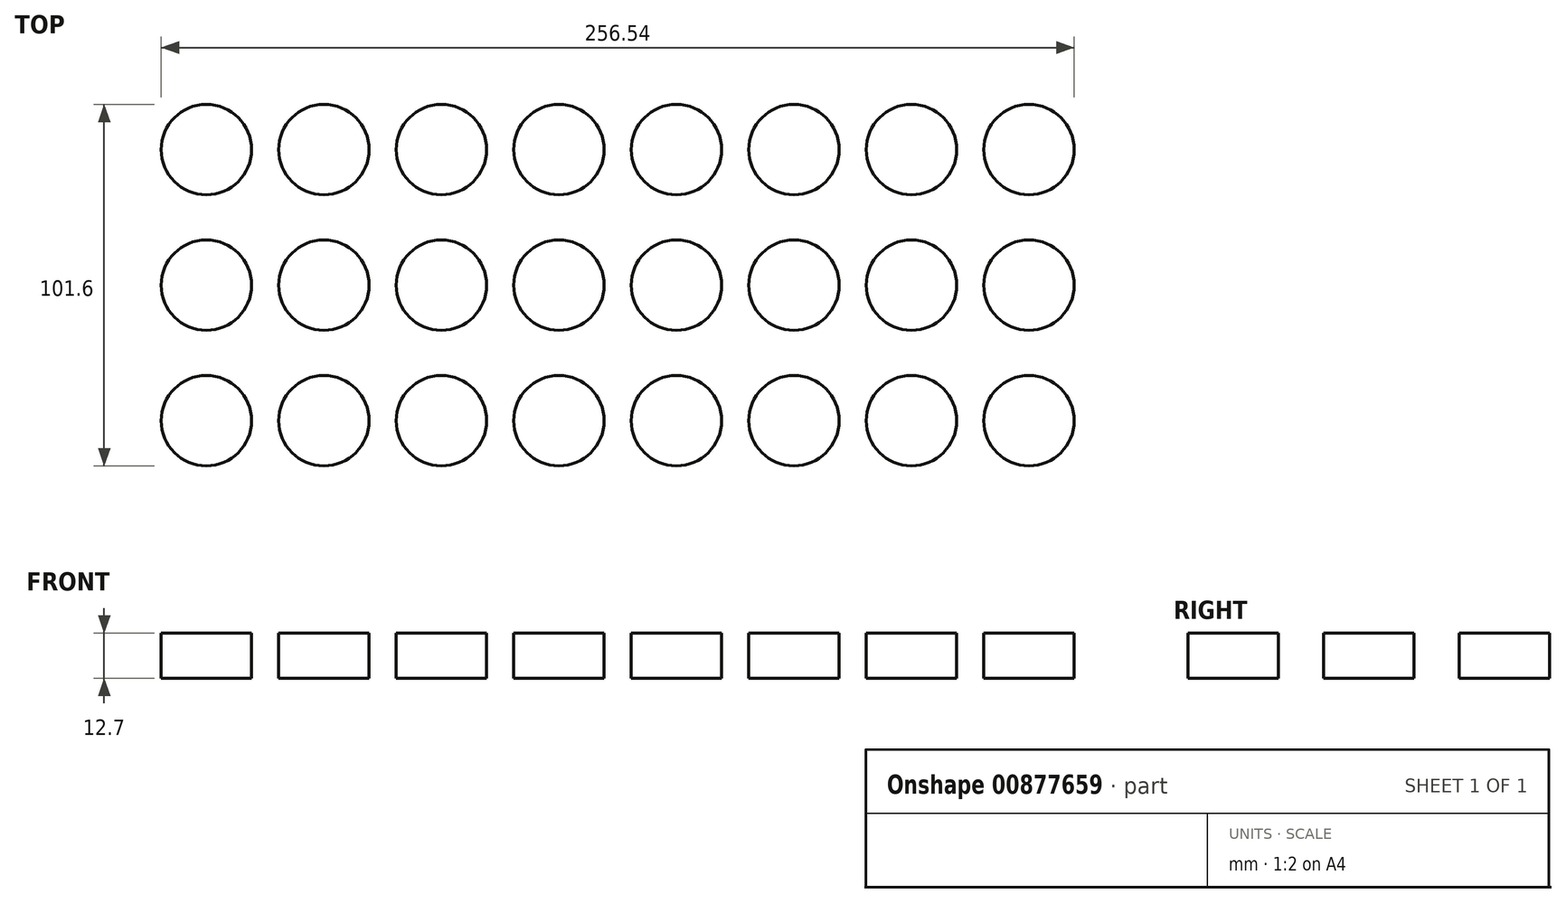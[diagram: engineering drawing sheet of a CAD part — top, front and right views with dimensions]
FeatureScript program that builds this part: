
annotation { "Feature Type Name" : "Feature", "Feature Type Description" : "" }
export const myFeature = defineFeature(function(context is Context, id is Id, definition is map)
    precondition{}
    {
        {
            var Q0;
            Q0=qCreatedBy(makeId("Top.planeOp"),FACE);
            var sketch = newSketch(context, id + "F0", { "sketchPlane" : qUnion([Q0])});
            skCircle(sketch, "E0", {"center": v(0, 0) * mm, "radius": 12.7 * mm});
            skCircle(sketch, "E1.0.1.0", {"center": v(0, 38.1) * mm, "radius": 12.7 * mm});
            skCircle(sketch, "E1.0.2.0", {"center": v(0, 76.2) * mm, "radius": 12.7 * mm});
            skCircle(sketch, "E1.1.0.0", {"center": v(33.02, 0) * mm, "radius": 12.7 * mm});
            skCircle(sketch, "E1.1.1.0", {"center": v(33.02, 38.1) * mm, "radius": 12.7 * mm});
            skCircle(sketch, "E1.1.2.0", {"center": v(33.02, 76.2) * mm, "radius": 12.7 * mm});
            skCircle(sketch, "E1.2.0.0", {"center": v(66.04, 0) * mm, "radius": 12.7 * mm});
            skCircle(sketch, "E1.2.1.0", {"center": v(66.04, 38.1) * mm, "radius": 12.7 * mm});
            skCircle(sketch, "E1.2.2.0", {"center": v(66.04, 76.2) * mm, "radius": 12.7 * mm});
            skCircle(sketch, "E1.3.0.0", {"center": v(99.06, 0) * mm, "radius": 12.7 * mm});
            skCircle(sketch, "E1.3.1.0", {"center": v(99.06, 38.1) * mm, "radius": 12.7 * mm});
            skCircle(sketch, "E1.3.2.0", {"center": v(99.06, 76.2) * mm, "radius": 12.7 * mm});
            skCircle(sketch, "E1.4.0.0", {"center": v(132.08, 0) * mm, "radius": 12.7 * mm});
            skCircle(sketch, "E1.4.1.0", {"center": v(132.08, 38.1) * mm, "radius": 12.7 * mm});
            skCircle(sketch, "E1.4.2.0", {"center": v(132.08, 76.2) * mm, "radius": 12.7 * mm});
            skCircle(sketch, "E1.5.0.0", {"center": v(165.1, 0) * mm, "radius": 12.7 * mm});
            skCircle(sketch, "E1.5.1.0", {"center": v(165.1, 38.1) * mm, "radius": 12.7 * mm});
            skCircle(sketch, "E1.5.2.0", {"center": v(165.1, 76.2) * mm, "radius": 12.7 * mm});
            skCircle(sketch, "E1.6.0.0", {"center": v(198.12, 0) * mm, "radius": 12.7 * mm});
            skCircle(sketch, "E1.6.1.0", {"center": v(198.12, 38.1) * mm, "radius": 12.7 * mm});
            skCircle(sketch, "E1.6.2.0", {"center": v(198.12, 76.2) * mm, "radius": 12.7 * mm});
            skCircle(sketch, "E1.7.0.0", {"center": v(231.14, 0) * mm, "radius": 12.7 * mm});
            skCircle(sketch, "E1.7.1.0", {"center": v(231.14, 38.1) * mm, "radius": 12.7 * mm});
            skCircle(sketch, "E1.7.2.0", {"center": v(231.14, 76.2) * mm, "radius": 12.7 * mm});
            skLineSegment(sketch, "E1.direction1", {"start": v(0, 0) * mm, "end": v(33.02, 0) * mm, "construction": true});
            skLineSegment(sketch, "E1.direction2", {"start": v(0, 0) * mm, "end": v(0, 38.1) * mm, "construction": true});
            skSolve(sketch);
        }
        {
            var Q0;
            Q0=makeQuery(id+"F0.imprint","IMPRINT",FACE,{"disambiguationData":[TD([[makeQuery(id+"F0.imprint","IMPRINT",EDGE,{"derivedFrom":sQuery(id+"F0.wireOp",EDGE,"E1.7.0.0")}),1.0]])]});
            var Q1;
            Q1=makeQuery(id+"F0.imprint","IMPRINT",FACE,{"disambiguationData":[TD([[makeQuery(id+"F0.imprint","IMPRINT",EDGE,{"derivedFrom":sQuery(id+"F0.wireOp",EDGE,"E1.6.0.0")}),1.0]])]});
            var Q2;
            Q2=makeQuery(id+"F0.imprint","IMPRINT",FACE,{"disambiguationData":[TD([[makeQuery(id+"F0.imprint","IMPRINT",EDGE,{"derivedFrom":sQuery(id+"F0.wireOp",EDGE,"E1.5.0.0")}),1.0]])]});
            var Q3;
            Q3=makeQuery(id+"F0.imprint","IMPRINT",FACE,{"disambiguationData":[TD([[makeQuery(id+"F0.imprint","IMPRINT",EDGE,{"derivedFrom":sQuery(id+"F0.wireOp",EDGE,"E1.4.0.0")}),1.0]])]});
            var Q4;
            Q4=makeQuery(id+"F0.imprint","IMPRINT",FACE,{"disambiguationData":[TD([[makeQuery(id+"F0.imprint","IMPRINT",EDGE,{"derivedFrom":sQuery(id+"F0.wireOp",EDGE,"E1.3.0.0")}),1.0]])]});
            var Q5;
            Q5=makeQuery(id+"F0.imprint","IMPRINT",FACE,{"disambiguationData":[TD([[makeQuery(id+"F0.imprint","IMPRINT",EDGE,{"derivedFrom":sQuery(id+"F0.wireOp",EDGE,"E1.1.0.0")}),1.0]])]});
            var Q6;
            Q6=makeQuery(id+"F0.imprint","IMPRINT",FACE,{"disambiguationData":[TD([[makeQuery(id+"F0.imprint","IMPRINT",EDGE,{"derivedFrom":sQuery(id+"F0.wireOp",EDGE,"E1.2.0.0")}),1.0]])]});
            var Q7;
            Q7=makeQuery(id+"F0.imprint","IMPRINT",FACE,{"disambiguationData":[TD([[makeQuery(id+"F0.imprint","IMPRINT",EDGE,{"derivedFrom":sQuery(id+"F0.wireOp",EDGE,"E0")}),1.0]])]});
            var Q8;
            Q8=makeQuery(id+"F0.imprint","IMPRINT",FACE,{"disambiguationData":[TD([[makeQuery(id+"F0.imprint","IMPRINT",EDGE,{"derivedFrom":sQuery(id+"F0.wireOp",EDGE,"E1.0.1.0")}),1.0]])]});
            var Q9;
            Q9=makeQuery(id+"F0.imprint","IMPRINT",FACE,{"disambiguationData":[TD([[makeQuery(id+"F0.imprint","IMPRINT",EDGE,{"derivedFrom":sQuery(id+"F0.wireOp",EDGE,"E1.1.1.0")}),1.0]])]});
            var Q10;
            Q10=makeQuery(id+"F0.imprint","IMPRINT",FACE,{"disambiguationData":[TD([[makeQuery(id+"F0.imprint","IMPRINT",EDGE,{"derivedFrom":sQuery(id+"F0.wireOp",EDGE,"E1.2.1.0")}),1.0]])]});
            var Q11;
            Q11=makeQuery(id+"F0.imprint","IMPRINT",FACE,{"disambiguationData":[TD([[makeQuery(id+"F0.imprint","IMPRINT",EDGE,{"derivedFrom":sQuery(id+"F0.wireOp",EDGE,"E1.3.1.0")}),1.0]])]});
            var Q12;
            Q12=makeQuery(id+"F0.imprint","IMPRINT",FACE,{"disambiguationData":[TD([[makeQuery(id+"F0.imprint","IMPRINT",EDGE,{"derivedFrom":sQuery(id+"F0.wireOp",EDGE,"E1.4.1.0")}),1.0]])]});
            var Q13;
            Q13=makeQuery(id+"F0.imprint","IMPRINT",FACE,{"disambiguationData":[TD([[makeQuery(id+"F0.imprint","IMPRINT",EDGE,{"derivedFrom":sQuery(id+"F0.wireOp",EDGE,"E1.5.1.0")}),1.0]])]});
            var Q14;
            Q14=makeQuery(id+"F0.imprint","IMPRINT",FACE,{"disambiguationData":[TD([[makeQuery(id+"F0.imprint","IMPRINT",EDGE,{"derivedFrom":sQuery(id+"F0.wireOp",EDGE,"E1.6.1.0")}),1.0]])]});
            var Q15;
            Q15=makeQuery(id+"F0.imprint","IMPRINT",FACE,{"disambiguationData":[TD([[makeQuery(id+"F0.imprint","IMPRINT",EDGE,{"derivedFrom":sQuery(id+"F0.wireOp",EDGE,"E1.7.1.0")}),1.0]])]});
            var Q16;
            Q16=makeQuery(id+"F0.imprint","IMPRINT",FACE,{"disambiguationData":[TD([[makeQuery(id+"F0.imprint","IMPRINT",EDGE,{"derivedFrom":sQuery(id+"F0.wireOp",EDGE,"E1.6.2.0")}),1.0]])]});
            var Q17;
            Q17=makeQuery(id+"F0.imprint","IMPRINT",FACE,{"disambiguationData":[TD([[makeQuery(id+"F0.imprint","IMPRINT",EDGE,{"derivedFrom":sQuery(id+"F0.wireOp",EDGE,"E1.5.2.0")}),1.0]])]});
            var Q18;
            Q18=makeQuery(id+"F0.imprint","IMPRINT",FACE,{"disambiguationData":[TD([[makeQuery(id+"F0.imprint","IMPRINT",EDGE,{"derivedFrom":sQuery(id+"F0.wireOp",EDGE,"E1.4.2.0")}),1.0]])]});
            var Q19;
            Q19=makeQuery(id+"F0.imprint","IMPRINT",FACE,{"disambiguationData":[TD([[makeQuery(id+"F0.imprint","IMPRINT",EDGE,{"derivedFrom":sQuery(id+"F0.wireOp",EDGE,"E1.3.2.0")}),1.0]])]});
            var Q20;
            Q20=makeQuery(id+"F0.imprint","IMPRINT",FACE,{"disambiguationData":[TD([[makeQuery(id+"F0.imprint","IMPRINT",EDGE,{"derivedFrom":sQuery(id+"F0.wireOp",EDGE,"E1.2.2.0")}),1.0]])]});
            var Q21;
            Q21=makeQuery(id+"F0.imprint","IMPRINT",FACE,{"disambiguationData":[TD([[makeQuery(id+"F0.imprint","IMPRINT",EDGE,{"derivedFrom":sQuery(id+"F0.wireOp",EDGE,"E1.1.2.0")}),1.0]])]});
            var Q22;
            Q22=makeQuery(id+"F0.imprint","IMPRINT",FACE,{"disambiguationData":[TD([[makeQuery(id+"F0.imprint","IMPRINT",EDGE,{"derivedFrom":sQuery(id+"F0.wireOp",EDGE,"E1.0.2.0")}),1.0]])]});
            var Q23;
            Q23=makeQuery(id+"F0.imprint","IMPRINT",FACE,{"disambiguationData":[TD([[makeQuery(id+"F0.imprint","IMPRINT",EDGE,{"derivedFrom":sQuery(id+"F0.wireOp",EDGE,"E1.0.3.0")}),1.0]])]});
            var Q24;
            Q24=makeQuery(id+"F0.imprint","IMPRINT",FACE,{"disambiguationData":[TD([[makeQuery(id+"F0.imprint","IMPRINT",EDGE,{"derivedFrom":sQuery(id+"F0.wireOp",EDGE,"E1.1.3.0")}),1.0]])]});
            var Q25;
            Q25=makeQuery(id+"F0.imprint","IMPRINT",FACE,{"disambiguationData":[TD([[makeQuery(id+"F0.imprint","IMPRINT",EDGE,{"derivedFrom":sQuery(id+"F0.wireOp",EDGE,"E1.2.3.0")}),1.0]])]});
            var Q26;
            Q26=makeQuery(id+"F0.imprint","IMPRINT",FACE,{"disambiguationData":[TD([[makeQuery(id+"F0.imprint","IMPRINT",EDGE,{"derivedFrom":sQuery(id+"F0.wireOp",EDGE,"E1.3.3.0")}),1.0]])]});
            var Q27;
            Q27=makeQuery(id+"F0.imprint","IMPRINT",FACE,{"disambiguationData":[TD([[makeQuery(id+"F0.imprint","IMPRINT",EDGE,{"derivedFrom":sQuery(id+"F0.wireOp",EDGE,"E1.4.3.0")}),1.0]])]});
            var Q28;
            Q28=makeQuery(id+"F0.imprint","IMPRINT",FACE,{"disambiguationData":[TD([[makeQuery(id+"F0.imprint","IMPRINT",EDGE,{"derivedFrom":sQuery(id+"F0.wireOp",EDGE,"E1.5.3.0")}),1.0]])]});
            var Q29;
            Q29=makeQuery(id+"F0.imprint","IMPRINT",FACE,{"disambiguationData":[TD([[makeQuery(id+"F0.imprint","IMPRINT",EDGE,{"derivedFrom":sQuery(id+"F0.wireOp",EDGE,"E1.6.3.0")}),1.0]])]});
            var Q30;
            Q30=makeQuery(id+"F0.imprint","IMPRINT",FACE,{"disambiguationData":[TD([[makeQuery(id+"F0.imprint","IMPRINT",EDGE,{"derivedFrom":sQuery(id+"F0.wireOp",EDGE,"E1.7.3.0")}),1.0]])]});
            var Q31;
            Q31=makeQuery(id+"F0.imprint","IMPRINT",FACE,{"disambiguationData":[TD([[makeQuery(id+"F0.imprint","IMPRINT",EDGE,{"derivedFrom":sQuery(id+"F0.wireOp",EDGE,"E1.7.2.0")}),1.0]])]});
            extrude(context, id + "F1", {"entities" : qUnion([Q0, Q1, Q2, Q3, Q4, Q5, Q6, Q7, Q8, Q9, Q10, Q11, Q12, Q13, Q14, Q15, Q16, Q17, Q18, Q19, Q20, Q21, Q22, Q23, Q24, Q25, Q26, Q27, Q28, Q29, Q30, Q31]), "depth" : 12.7 * mm, "offsetDistance" : 25.4 * mm});
        }
    });
